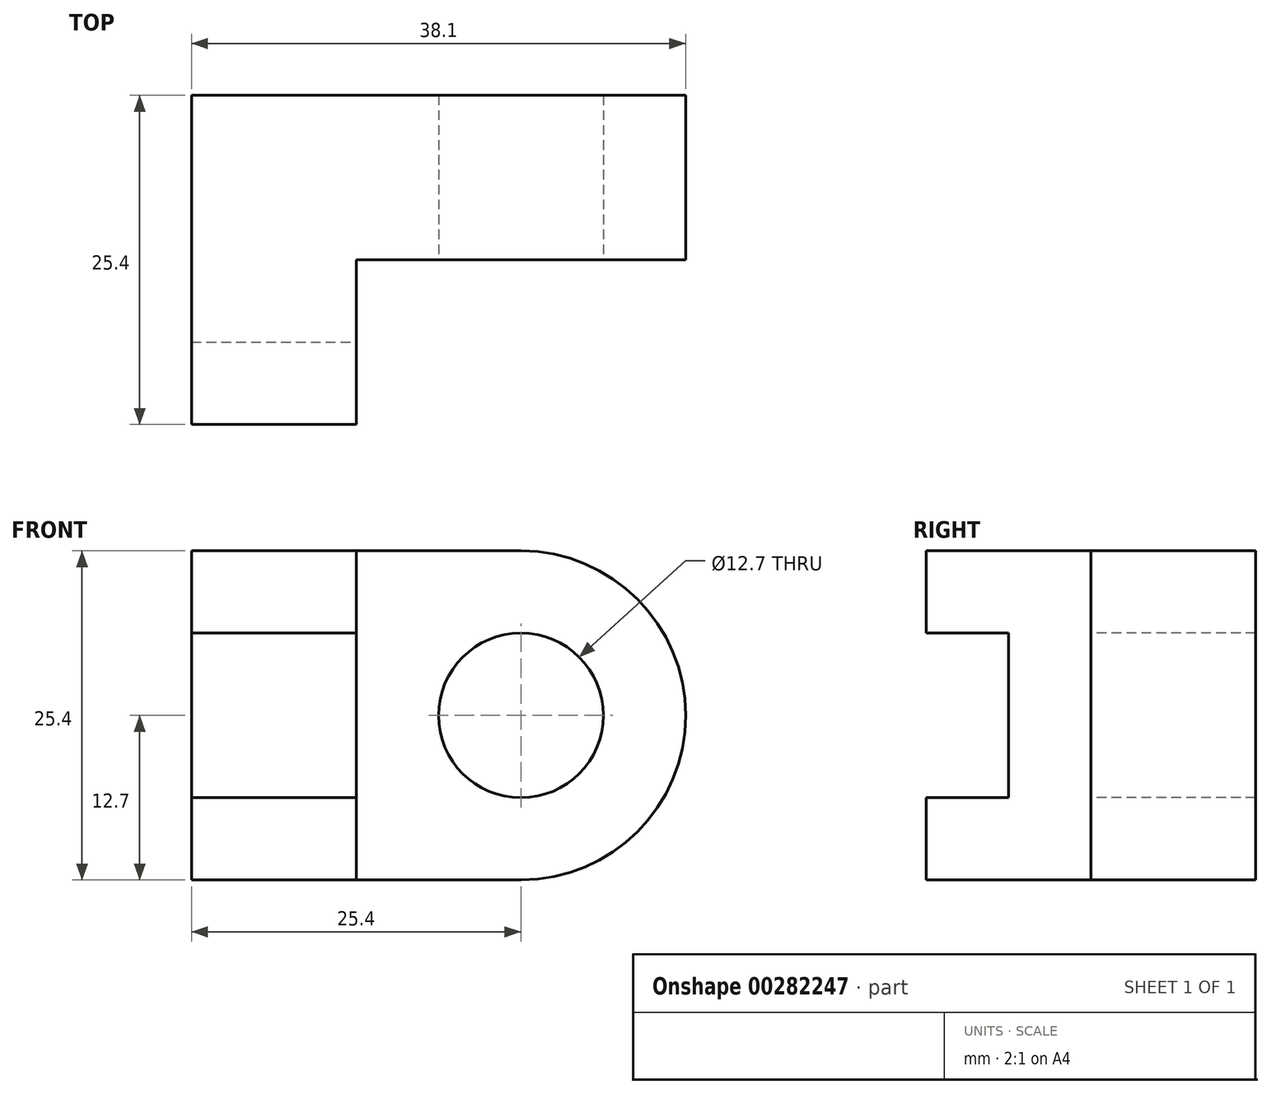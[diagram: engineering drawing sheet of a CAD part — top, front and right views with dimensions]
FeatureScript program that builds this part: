
annotation { "Feature Type Name" : "Feature", "Feature Type Description" : "" }
export const myFeature = defineFeature(function(context is Context, id is Id, definition is map)
    precondition{}
    {
        {
            var Q0;
            Q0=qCreatedBy(makeId("Right.planeOp"),FACE);
            var sketch = newSketch(context, id + "F0", { "sketchPlane" : qUnion([Q0])});
            skLineSegment(sketch, "E0.bottom", {"start": v(0, 0) * mm, "end": v(-25.4, 0) * mm});
            skLineSegment(sketch, "E0.top", {"start": v(0, 25.4) * mm, "end": v(-25.4, 25.4) * mm});
            skLineSegment(sketch, "E0.left", {"start": v(0, 0) * mm, "end": v(0, 25.4) * mm});
            skLineSegment(sketch, "E0.right", {"start": v(-25.4, 0) * mm, "end": v(-25.4, 25.4) * mm});
            skSolve(sketch);
        }
        {
            var Q0;
            Q0 = qSketchRegion(id + "F0", true);
            extrude(context, id + "F1", {"entities" : qUnion([Q0]), "endBound" : BoundingType.SYMMETRIC, "depth" : 12.7 * mm});
        }
        {
            var Q0;
            Q0=qCreatedBy(makeId("Right.planeOp"),FACE);
            var sketch = newSketch(context, id + "F2", { "sketchPlane" : qUnion([Q0])});
            skLineSegment(sketch, "E1.bottom", {"start": v(-25.4, 19.05) * mm, "end": v(-19.05, 19.05) * mm});
            skLineSegment(sketch, "E1.top", {"start": v(-25.4, 6.35) * mm, "end": v(-19.05, 6.35) * mm});
            skLineSegment(sketch, "E1.left", {"start": v(-25.4, 19.05) * mm, "end": v(-25.4, 6.35) * mm});
            skLineSegment(sketch, "E1.right", {"start": v(-19.05, 19.05) * mm, "end": v(-19.05, 6.35) * mm});
            skSolve(sketch);
        }
        {
            var Q0;
            Q0 = qSketchRegion(id + "F2", true);
            extrude(context, id + "F3", {"entities" : qUnion([Q0]), "operationType" : NewBodyOperationType.REMOVE, "endBound" : BoundingType.SYMMETRIC, "oppositeDirection" : true, "depth" : 12.7 * mm});
        }
        {
            var Q0;
            Q0=makeQuery(id+"F1.opExtrude","CAP_FACE",FACE,{"disambiguationData":[OSD([sQuery(id+"F0.wireOp",EDGE,"E0.bottom"),sQuery(id+"F0.wireOp",EDGE,"E0.top"),sQuery(id+"F0.wireOp",EDGE,"E0.left"),sQuery(id+"F0.wireOp",EDGE,"E0.right")])],"isStart":false});
            var sketch = newSketch(context, id + "F4", { "sketchPlane" : qUnion([Q0])});
            skLineSegment(sketch, "E2.bottom", {"start": v(0, 25.4) * mm, "end": v(-12.7, 25.4) * mm});
            skLineSegment(sketch, "E2.top", {"start": v(0, 0) * mm, "end": v(-12.7, 0) * mm});
            skLineSegment(sketch, "E2.left", {"start": v(0, 25.4) * mm, "end": v(0, 0) * mm});
            skLineSegment(sketch, "E2.right", {"start": v(-12.7, 25.4) * mm, "end": v(-12.7, 0) * mm});
            skSolve(sketch);
        }
        {
            var Q0;
            Q0 = qSketchRegion(id + "F4", true);
            extrude(context, id + "F5", {"entities" : qUnion([Q0]), "operationType" : NewBodyOperationType.ADD, "depth" : 12.7 * mm});
        }
        {
            var Q0;
            Q0=makeQuery(id+"F5.boolean.opBoolean","MERGE",FACE,{"derivedFrom":[makeQuery(id+"F1.opExtrude","SWEPT_FACE",FACE,{"disambiguationData":[OSD([sQuery(id+"F0.wireOp",EDGE,"E0.left")])]}),makeQuery(id+"F5.opExtrude","SWEPT_FACE",FACE,{"disambiguationData":[OSD([sQuery(id+"F4.wireOp",EDGE,"E2.left")])]})]});
            var sketch = newSketch(context, id + "F6", { "sketchPlane" : qUnion([Q0])});
            skArc(sketch, "E3", {"start": v(-19.05, 25.4) * mm, "mid": v(-31.75, 12.7) * mm, "end": v(-19.05, 0) * mm});
            skSolve(sketch);
        }
        {
            var Q0;
            Q0=makeQuery(id+"F6.imprint","IMPRINT",FACE,{"disambiguationData":[TD([[makeQuery(id+"F6.imprint","IMPRINT",EDGE,{"derivedFrom":sQuery(id+"F6.wireOp",EDGE,"E3")}),1.0]])]});
            extrude(context, id + "F7", {"entities" : qUnion([Q0]), "operationType" : NewBodyOperationType.ADD, "oppositeDirection" : true, "depth" : 12.7 * mm});
        }
        {
            var Q0;
            Q0=makeQuery(id+"F7.boolean.opBoolean","MERGE",FACE,{"derivedFrom":[makeQuery(id+"F5.opExtrude","SWEPT_FACE",FACE,{"disambiguationData":[OSD([sQuery(id+"F4.wireOp",EDGE,"E2.right")])]}),makeQuery(id+"F7.opExtrude","CAP_FACE",FACE,{"disambiguationData":[OSD([sQuery(id+"F4.wireOp",EDGE,"E2.left"),sQuery(id+"F6.wireOp",EDGE,"E3")])],"isStart":false})]});
            var sketch = newSketch(context, id + "F8", { "sketchPlane" : qUnion([Q0])});
            skCircle(sketch, "E4", {"center": v(19.05, 12.7) * mm, "radius": 6.35 * mm});
            skSolve(sketch);
        }
        {
            var Q0;
            Q0 = qSketchRegion(id + "F8", true);
            extrude(context, id + "F9", {"entities" : qUnion([Q0]), "operationType" : NewBodyOperationType.REMOVE, "oppositeDirection" : true, "depth" : 12.7 * mm});
        }
    });
